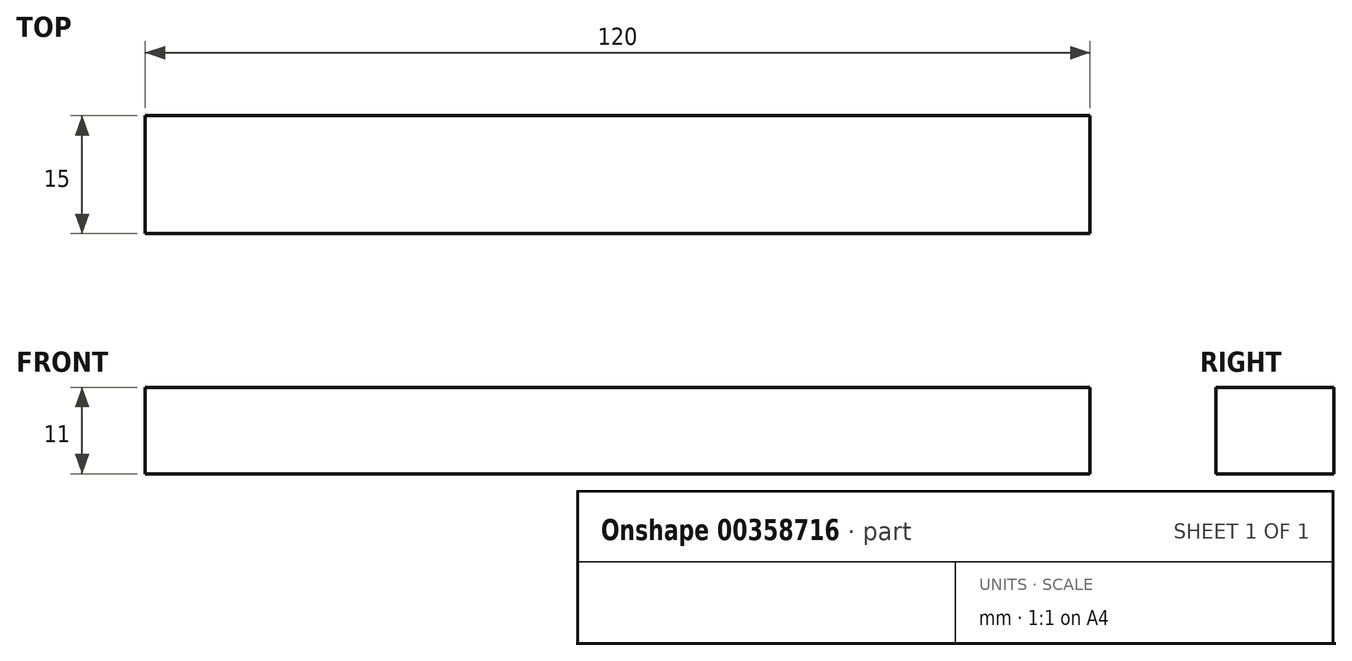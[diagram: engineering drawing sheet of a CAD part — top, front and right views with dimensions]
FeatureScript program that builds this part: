
annotation { "Feature Type Name" : "Feature", "Feature Type Description" : "" }
export const myFeature = defineFeature(function(context is Context, id is Id, definition is map)
    precondition{}
    {
        {
            var Q0;
            Q0=qCreatedBy(makeId("Right.planeOp"),FACE);
            var sketch = newSketch(context, id + "F0", { "sketchPlane" : qUnion([Q0])});
            skLineSegment(sketch, "E0.bottom", {"start": v(7.5, -5.5) * mm, "end": v(-7.5, -5.5) * mm});
            skLineSegment(sketch, "E0.top", {"start": v(7.5, 5.5) * mm, "end": v(-7.5, 5.5) * mm});
            skLineSegment(sketch, "E0.left", {"start": v(7.5, -5.5) * mm, "end": v(7.5, 5.5) * mm});
            skLineSegment(sketch, "E0.right", {"start": v(-7.5, -5.5) * mm, "end": v(-7.5, 5.5) * mm});
            skPoint(sketch, "E0.middle", {"position": v(0, 0) * mm});
            skSolve(sketch);
        }
        {
            var Q0;
            Q0 = qSketchRegion(id + "F0", true);
            extrude(context, id + "F1", {"entities" : qUnion([Q0]), "depth" : 120 * mm});
        }
    });
